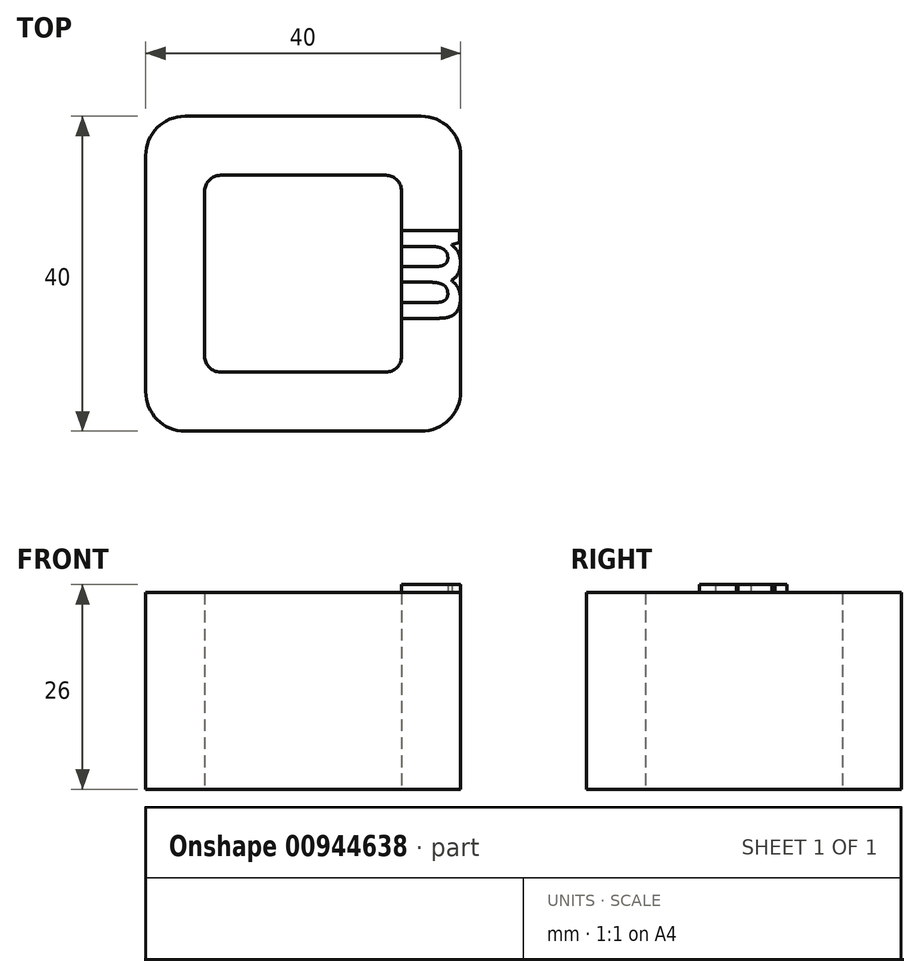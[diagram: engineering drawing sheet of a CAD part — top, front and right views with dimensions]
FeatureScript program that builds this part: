
annotation { "Feature Type Name" : "Feature", "Feature Type Description" : "" }
export const myFeature = defineFeature(function(context is Context, id is Id, definition is map)
    precondition{}
    {
        {
            var Q0;
            Q0=qCreatedBy(makeId("Top.planeOp"),FACE);
            var sketch = newSketch(context, id + "F0", { "sketchPlane" : qUnion([Q0])});
            skLineSegment(sketch, "E0.bottom", {"start": v(-15, 20) * mm, "end": v(15, 20) * mm});
            skLineSegment(sketch, "E0.top", {"start": v(-15, -20) * mm, "end": v(15, -20) * mm});
            skLineSegment(sketch, "E0.left", {"start": v(-20, 15) * mm, "end": v(-20, -15) * mm});
            skLineSegment(sketch, "E0.right", {"start": v(20, 15) * mm, "end": v(20, -15) * mm});
            skPoint(sketch, "E0.middle", {"position": v(0, 0) * mm});
            skPoint(sketch, "E1.visualSharp", {"position": v(-20, 20) * mm});
            skArc(sketch, "E1.filletArc", {"start": v(-15, 20) * mm, "mid": v(-18.54, 18.54) * mm, "end": v(-20, 15) * mm});
            skPoint(sketch, "E2.visualSharp", {"position": v(20, 20) * mm});
            skArc(sketch, "E2.filletArc", {"start": v(20, 15) * mm, "mid": v(18.54, 18.54) * mm, "end": v(15, 20) * mm});
            skPoint(sketch, "E3.visualSharp", {"position": v(20, -20) * mm});
            skArc(sketch, "E3.filletArc", {"start": v(15, -20) * mm, "mid": v(18.54, -18.54) * mm, "end": v(20, -15) * mm});
            skPoint(sketch, "E4.visualSharp", {"position": v(-20, -20) * mm});
            skArc(sketch, "E4.filletArc", {"start": v(-20, -15) * mm, "mid": v(-18.54, -18.54) * mm, "end": v(-15, -20) * mm});
            skLineSegment(sketch, "E5.0", {"start": v(12.5, 10.5) * mm, "end": v(12.5, -10.5) * mm});
            skLineSegment(sketch, "E5.1", {"start": v(-10.5, 12.5) * mm, "end": v(10.5, 12.5) * mm});
            skLineSegment(sketch, "E5.2", {"start": v(-12.5, 10.5) * mm, "end": v(-12.5, -10.5) * mm});
            skLineSegment(sketch, "E5.3", {"start": v(-10.5, -12.5) * mm, "end": v(10.5, -12.5) * mm});
            skPoint(sketch, "E6.visualSharp", {"position": v(-12.5, 12.5) * mm});
            skArc(sketch, "E6.filletArc", {"start": v(-10.5, 12.5) * mm, "mid": v(-11.91, 11.91) * mm, "end": v(-12.5, 10.5) * mm});
            skPoint(sketch, "E7.visualSharp", {"position": v(12.5, 12.5) * mm});
            skArc(sketch, "E7.filletArc", {"start": v(12.5, 10.5) * mm, "mid": v(11.91, 11.91) * mm, "end": v(10.5, 12.5) * mm});
            skPoint(sketch, "E8.visualSharp", {"position": v(12.5, -12.5) * mm});
            skArc(sketch, "E8.filletArc", {"start": v(10.5, -12.5) * mm, "mid": v(11.91, -11.91) * mm, "end": v(12.5, -10.5) * mm});
            skPoint(sketch, "E9.visualSharp", {"position": v(-12.5, -12.5) * mm});
            skArc(sketch, "E9.filletArc", {"start": v(-12.5, -10.5) * mm, "mid": v(-11.91, -11.91) * mm, "end": v(-10.5, -12.5) * mm});
            skSolve(sketch);
        }
        {
            var Q0;
            Q0=qCreatedBy(makeId("Top.planeOp"),FACE);
            var sketch = newSketch(context, id + "F1", { "sketchPlane" : qUnion([Q0])});
            skPoint(sketch, "E10.secondSnap0", {"position": v(28.4, -17.64) * mm});
            skText(sketch, "E11", { "text": "m", "fontName": "OpenSans-Bold.ttf"});
            const initialGuessF1  = {"E11": [0.0125, 0.00653, 0, -1, 0.00968]};
            skSetInitialGuess(sketch, initialGuessF1);
            skSolve(sketch);
        }
        {
            var Q0;
            Q0 = qSketchRegion(id + "F0", true);
            extrude(context, id + "F2", {"entities" : qUnion([Q0]), "depth" : 25 * mm, "offsetDistance" : 25 * mm});
        }
        {
            var Q0;
            Q0 = qSketchRegion(id + "F1", true);
            extrude(context, id + "F3", {"entities" : qUnion([Q0]), "operationType" : NewBodyOperationType.ADD, "depth" : 26 * mm, "offsetDistance" : 25 * mm});
        }
    });
